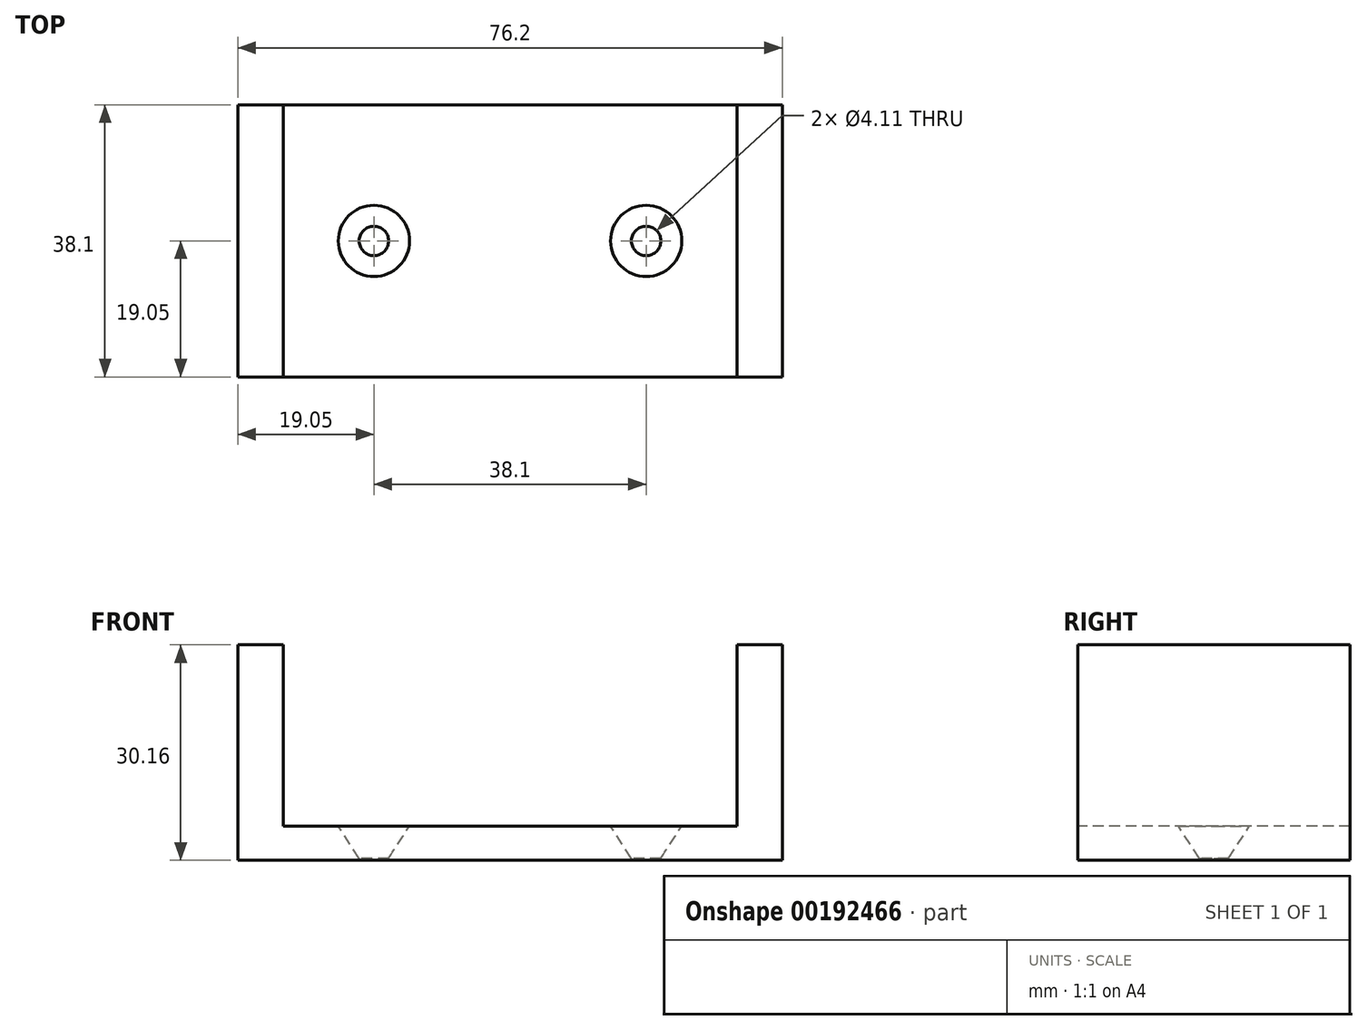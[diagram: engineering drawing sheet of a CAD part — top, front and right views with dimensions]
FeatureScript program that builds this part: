
annotation { "Feature Type Name" : "Feature", "Feature Type Description" : "" }
export const myFeature = defineFeature(function(context is Context, id is Id, definition is map)
    precondition{}
    {
        {
            var Q0;
            Q0=qCreatedBy(makeId("Top.planeOp"),FACE);
            var sketch = newSketch(context, id + "F0", { "sketchPlane" : qUnion([Q0])});
            skLineSegment(sketch, "E0.bottom", {"start": v(38.1, 19.05) * mm, "end": v(-38.1, 19.05) * mm});
            skLineSegment(sketch, "E0.top", {"start": v(38.1, -19.05) * mm, "end": v(-38.1, -19.05) * mm});
            skLineSegment(sketch, "E0.left", {"start": v(38.1, 19.05) * mm, "end": v(38.1, -19.05) * mm});
            skLineSegment(sketch, "E0.right", {"start": v(-38.1, 19.05) * mm, "end": v(-38.1, -19.05) * mm});
            skPoint(sketch, "E0.middle", {"position": v(0, 0) * mm});
            skCircle(sketch, "E1", {"center": v(-19.05, 0) * mm, "radius": 2.06 * mm});
            skCircle(sketch, "E2", {"center": v(19.05, 0) * mm, "radius": 2.06 * mm});
            skSolve(sketch);
        }
        {
            var Q0;
            Q0 = qSketchRegion(id + "F0", true);
            extrude(context, id + "F1", {"entities" : qUnion([Q0]), "depth" : 4.76 * mm});
        }
        {
            var Q0;
            Q0=makeQuery(id+"F1.opExtrude","CAP_FACE",FACE,{"disambiguationData":[OSD([sQuery(id+"F0.wireOp",EDGE,"E0.bottom"),sQuery(id+"F0.wireOp",EDGE,"E0.top"),sQuery(id+"F0.wireOp",EDGE,"E0.left"),sQuery(id+"F0.wireOp",EDGE,"E0.right")])],"isStart":false});
            var sketch = newSketch(context, id + "F2", { "sketchPlane" : qUnion([Q0])});
            skLineSegment(sketch, "E3", {"start": v(-38.1, -19.05) * mm, "end": v(-31.75, -19.05) * mm});
            skLineSegment(sketch, "E4", {"start": v(-31.75, -19.05) * mm, "end": v(-31.75, 19.05) * mm});
            skLineSegment(sketch, "E5", {"start": v(-31.75, 19.05) * mm, "end": v(-38.1, 19.05) * mm});
            skLineSegment(sketch, "E6", {"start": v(-38.1, 19.05) * mm, "end": v(-38.1, -19.05) * mm});
            skLineSegment(sketch, "E7", {"start": v(31.75, -19.05) * mm, "end": v(38.1, -19.05) * mm});
            skLineSegment(sketch, "E8", {"start": v(38.1, -19.05) * mm, "end": v(38.1, 19.05) * mm});
            skLineSegment(sketch, "E9", {"start": v(38.1, 19.05) * mm, "end": v(31.75, 19.05) * mm});
            skLineSegment(sketch, "E10", {"start": v(31.75, 19.05) * mm, "end": v(31.75, -19.05) * mm});
            skSolve(sketch);
        }
        {
            var Q0;
            Q0 = qSketchRegion(id + "F2", true);
            extrude(context, id + "F3", {"entities" : qUnion([Q0]), "operationType" : NewBodyOperationType.ADD, "depth" : 25.4 * mm});
        }
        {
            var Q0;
            Q0=makeQuery(id+"F1.opExtrude","CAP_EDGE",EDGE,{"disambiguationData":[OSD([sQuery(id+"F0.wireOp",EDGE,"E1")])],"isStart":false});
            chamfer(context, id + "F4", {"entities" : qUnion([Q0]), "chamferType" : ChamferType.TWO_OFFSETS, "width1" : 4.47 * mm, "oppositeDirection" : false, "width2" : 2.92 * mm, "tangentPropagation" : true});
        }
        {
            var Q0;
            Q0=makeQuery(id+"F1.opExtrude","CAP_EDGE",EDGE,{"disambiguationData":[OSD([sQuery(id+"F0.wireOp",EDGE,"E2")])],"isStart":false});
            chamfer(context, id + "F5", {"entities" : qUnion([Q0]), "chamferType" : ChamferType.TWO_OFFSETS, "width1" : 4.47 * mm, "oppositeDirection" : false, "width2" : 2.92 * mm, "tangentPropagation" : true});
        }
    });
